# Revit family: 591_SH-A_nailfin
name_source: partatom
category: Windows
revit_build: Autodesk Revit 2016 (Build: 20150220_1215(x64)
units: mm (PartAtom-declared; Revit-internal decimal feet)

## family parameters
Always vertical = Yes
Cut with Voids When Loaded = No
Host = Wall
OmniClass Number = 23.30.20.00
OmniClass Title = Windows
Room Calculation Point = No
Shared = No

## types (66) — shared parameters
Default Sill Height = 31 1/2"
Wall Closure = By host

## per-type parameters (varying)
| type | BSL | BSU | Height | MLW | Width |
| 24x72 | 24" | 24" | 72" | 3" | 24" |
| 12x36Min | 12" | 12" | 36" | 1 1/2" | 12" |
| 48x108Max | 36" | 36" | 108" | 6" | 48" |
| 36x96 | 32" | 32" | 96" | 4 1/2" | 36" |
| 12x42 | 14" | 14" | 42" | 1 1/2" | 12" |
| 12x48 | 16" | 16" | 48" | 1 1/2" | 12" |
| 12x54 | 18" | 18" | 54" | 1 1/2" | 12" |
| 12x60 | 20" | 20" | 60" | 1 1/2" | 12" |
| 18x36 | 12" | 12" | 36" | 2 1/4" | 18" |
| 18x42 | 14" | 14" | 42" | 2 1/4" | 18" |
| 18x48 | 16" | 16" | 48" | 2 1/4" | 18" |
| 18x54 | 18" | 18" | 54" | 2 1/4" | 18" |
| 18x60 | 20" | 20" | 60" | 2 1/4" | 18" |
| 18x66 | 22" | 22" | 66" | 2 1/4" | 18" |
| 18x72 | 24" | 24" | 72" | 2 1/4" | 18" |
| 18x78 | 26" | 26" | 78" | 2 1/4" | 18" |
| 24x42 | 14" | 14" | 42" | 3" | 24" |
| 24x48 | 16" | 16" | 48" | 3" | 24" |
| 24x54 | 18" | 18" | 54" | 3" | 24" |
| 24x60 | 20" | 20" | 60" | 3" | 24" |
| 24x66 | 22" | 22" | 66" | 3" | 24" |
| 24x78 | 26" | 26" | 78" | 3" | 24" |
| 24x84 | 28" | 28" | 84" | 3" | 24" |
| 24x90 | 30" | 30" | 90" | 3" | 24" |
| 24x96 | 32" | 32" | 96" | 3" | 24" |
| 30x42 | 14" | 14" | 42" | 3 3/4" | 30" |
| 30x48 | 16" | 16" | 48" | 3 3/4" | 30" |
| 30x54 | 18" | 18" | 54" | 3 3/4" | 30" |
| 30x60 | 20" | 20" | 60" | 3 3/4" | 30" |
| 30x66 | 22" | 22" | 66" | 3 3/4" | 30" |
| 30x72 | 24" | 24" | 72" | 3 3/4" | 30" |
| 30x78 | 26" | 26" | 78" | 3 3/4" | 30" |
| 30x84 | 28" | 28" | 84" | 3 3/4" | 30" |
| 30x90 | 30" | 30" | 90" | 3 3/4" | 30" |
| 30x96 | 32" | 32" | 96" | 3 3/4" | 30" |
| 30x102 | 34" | 34" | 102" | 3 3/4" | 30" |
| 36x48 | 16" | 16" | 48" | 4 1/2" | 36" |
| 36x54 | 18" | 18" | 54" | 4 1/2" | 36" |
| 36x60 | 20" | 20" | 60" | 4 1/2" | 36" |
| 36x66 | 22" | 22" | 66" | 4 1/2" | 36" |
| 36x72 | 24" | 24" | 72" | 4 1/2" | 36" |
| 36x78 | 26" | 26" | 78" | 4 1/2" | 36" |
| 36x84 | 28" | 28" | 84" | 4 1/2" | 36" |
| 36x90 | 30" | 30" | 90" | 4 1/2" | 36" |
| 36x102 | 34" | 34" | 102" | 4 1/2" | 36" |
| 36x108 | 36" | 36" | 108" | 4 1/2" | 36" |
| 42x48 | 16" | 16" | 48" | 5 1/4" | 42" |
| 42x54 | 18" | 18" | 54" | 5 1/4" | 42" |
| 42x60 | 20" | 20" | 60" | 5 1/4" | 42" |
| 42x66 | 22" | 22" | 66" | 5 1/4" | 42" |
| 42x72 | 24" | 24" | 72" | 5 1/4" | 42" |
| 42x78 | 26" | 26" | 78" | 5 1/4" | 42" |
| 42x84 | 28" | 28" | 84" | 5 1/4" | 42" |
| 42x90 | 30" | 30" | 90" | 5 1/4" | 42" |
| 42x96 | 32" | 32" | 96" | 5 1/4" | 42" |
| 42x102 | 34" | 34" | 102" | 5 1/4" | 42" |
| 42x108 | 36" | 36" | 108" | 5 1/4" | 42" |
| 48x54 | 18" | 18" | 54" | 6" | 48" |
| 48x60 | 20" | 20" | 60" | 6" | 48" |
| 48x66 | 22" | 22" | 66" | 6" | 48" |
| 48x72 | 24" | 24" | 72" | 6" | 48" |
| 48x78 | 26" | 26" | 78" | 6" | 48" |
| 48x84 | 28" | 28" | 84" | 6" | 48" |
| 48x90 | 30" | 30" | 90" | 6" | 48" |
| 48x96 | 32" | 32" | 96" | 6" | 48" |
| 48x102 | 34" | 34" | 102" | 6" | 48" |

## geometry (parser evidence)
native form markers: Sweep x2
no freeform markers — native parametric forms only
